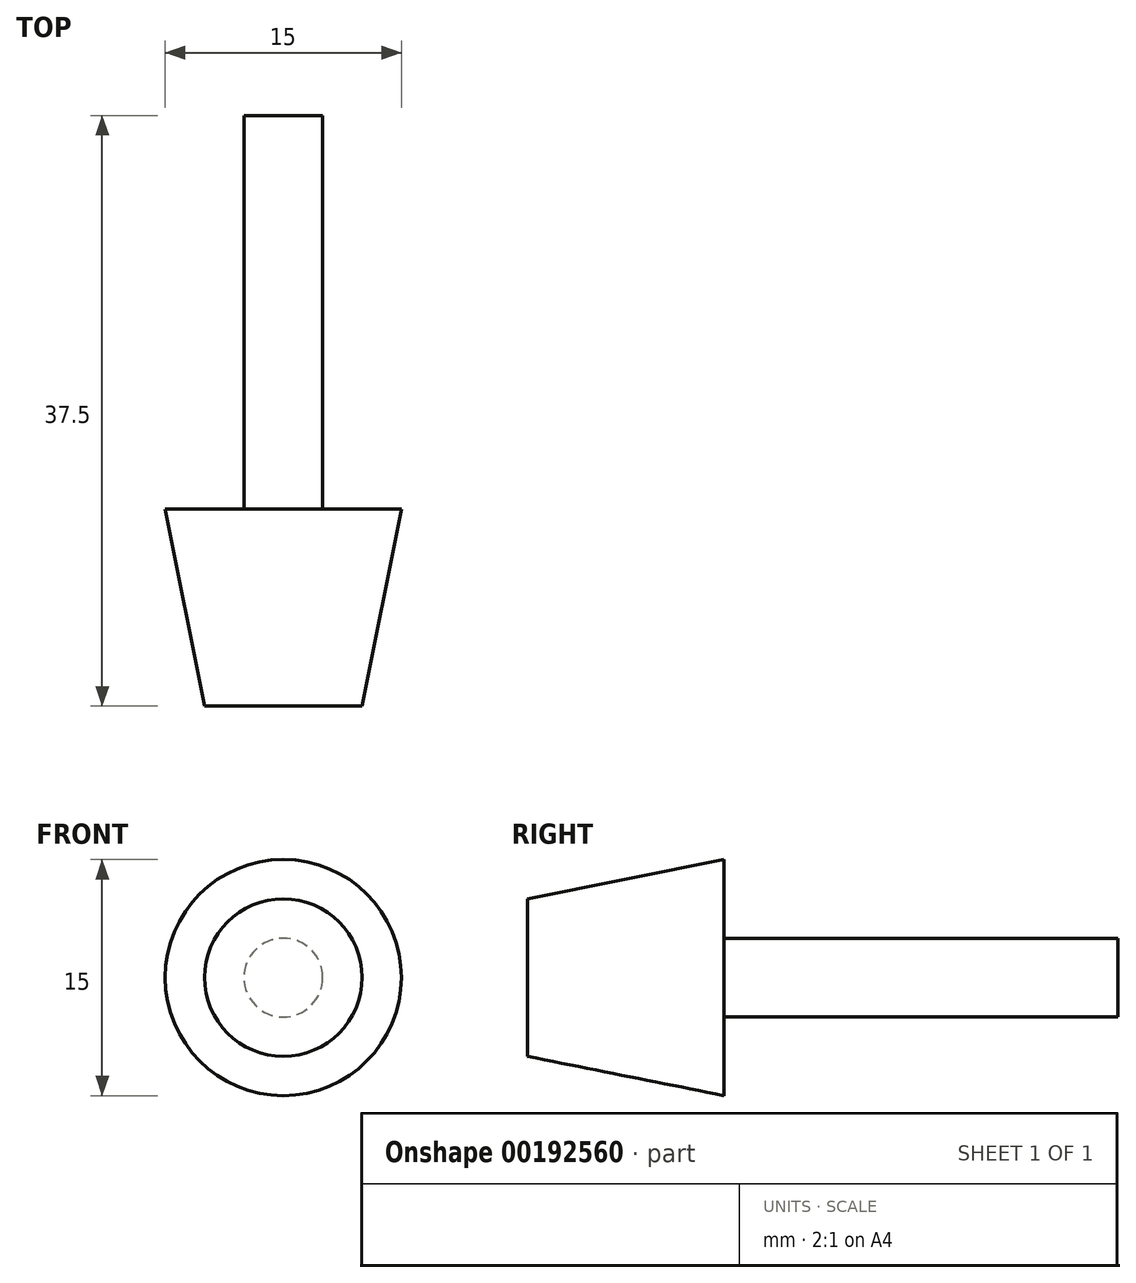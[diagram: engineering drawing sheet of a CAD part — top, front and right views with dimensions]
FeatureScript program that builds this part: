
annotation { "Feature Type Name" : "Feature", "Feature Type Description" : "" }
export const myFeature = defineFeature(function(context is Context, id is Id, definition is map)
    precondition{}
    {
        {
            var Q0;
            Q0=qCreatedBy(makeId("Front.planeOp"),FACE);
            var sketch = newSketch(context, id + "F0", { "sketchPlane" : qUnion([Q0])});
            skCircle(sketch, "E0", {"center": v(0, 0) * mm, "radius": 5 * mm});
            skSolve(sketch);
        }
        {
            var Q0;
            Q0=qCreatedBy(makeId("Front.planeOp"),FACE);
            cPlane(context, id + "F1", {"entities" : qUnion([Q0]), "cplaneType" : CPlaneType.OFFSET, "offset" : 12.5 * mm, "oppositeDirection" : true, "width" : 150 * mm, "height" : 150 * mm});
        }
        {
            var Q0;
            Q0=qCreatedBy(id+"F1.planeOp",FACE);
            var sketch = newSketch(context, id + "F2", { "sketchPlane" : qUnion([Q0])});
            skCircle(sketch, "E1", {"center": v(0, 0) * mm, "radius": 7.5 * mm});
            skSolve(sketch);
        }
        {
            var Q0;
            Q0=makeQuery(id+"F2.imprint","IMPRINT",FACE,{"disambiguationData":[TD([[makeQuery(id+"F2.imprint","IMPRINT",EDGE,{"derivedFrom":sQuery(id+"F2.wireOp",EDGE,"E1")}),1.0]])]});
            var Q1;
            Q1=makeQuery(id+"F0.imprint","IMPRINT",FACE,{"disambiguationData":[TD([[makeQuery(id+"F0.imprint","IMPRINT",EDGE,{"derivedFrom":sQuery(id+"F0.wireOp",EDGE,"E0")}),1.0]])]});
            loft(context, id + "F3", {"sheetProfilesArray" : [{ "sheetProfileEntities" : qUnion([Q0]) }, { "sheetProfileEntities" : qUnion([Q1]) }]});
        }
        {
            var Q0;
            Q0=makeQuery(id+"F3.opLoft","CAP_FACE",FACE,{"disambiguationData":[OSD([makeQuery(id+"F2.imprint","IMPRINT",FACE,{"disambiguationData":[TD([[makeQuery(id+"F2.imprint","IMPRINT",EDGE,{"derivedFrom":sQuery(id+"F2.wireOp",EDGE,"E1")}),1.0]])]})])],"isStart":true});
            var sketch = newSketch(context, id + "F4", { "sketchPlane" : qUnion([Q0])});
            skCircle(sketch, "E2", {"center": v(0, 0) * mm, "radius": 2.5 * mm});
            skSolve(sketch);
        }
        {
            var Q0;
            Q0 = qSketchRegion(id + "F4", true);
            extrude(context, id + "F5", {"entities" : qUnion([Q0]), "operationType" : NewBodyOperationType.ADD, "depth" : 25 * mm});
        }
    });
